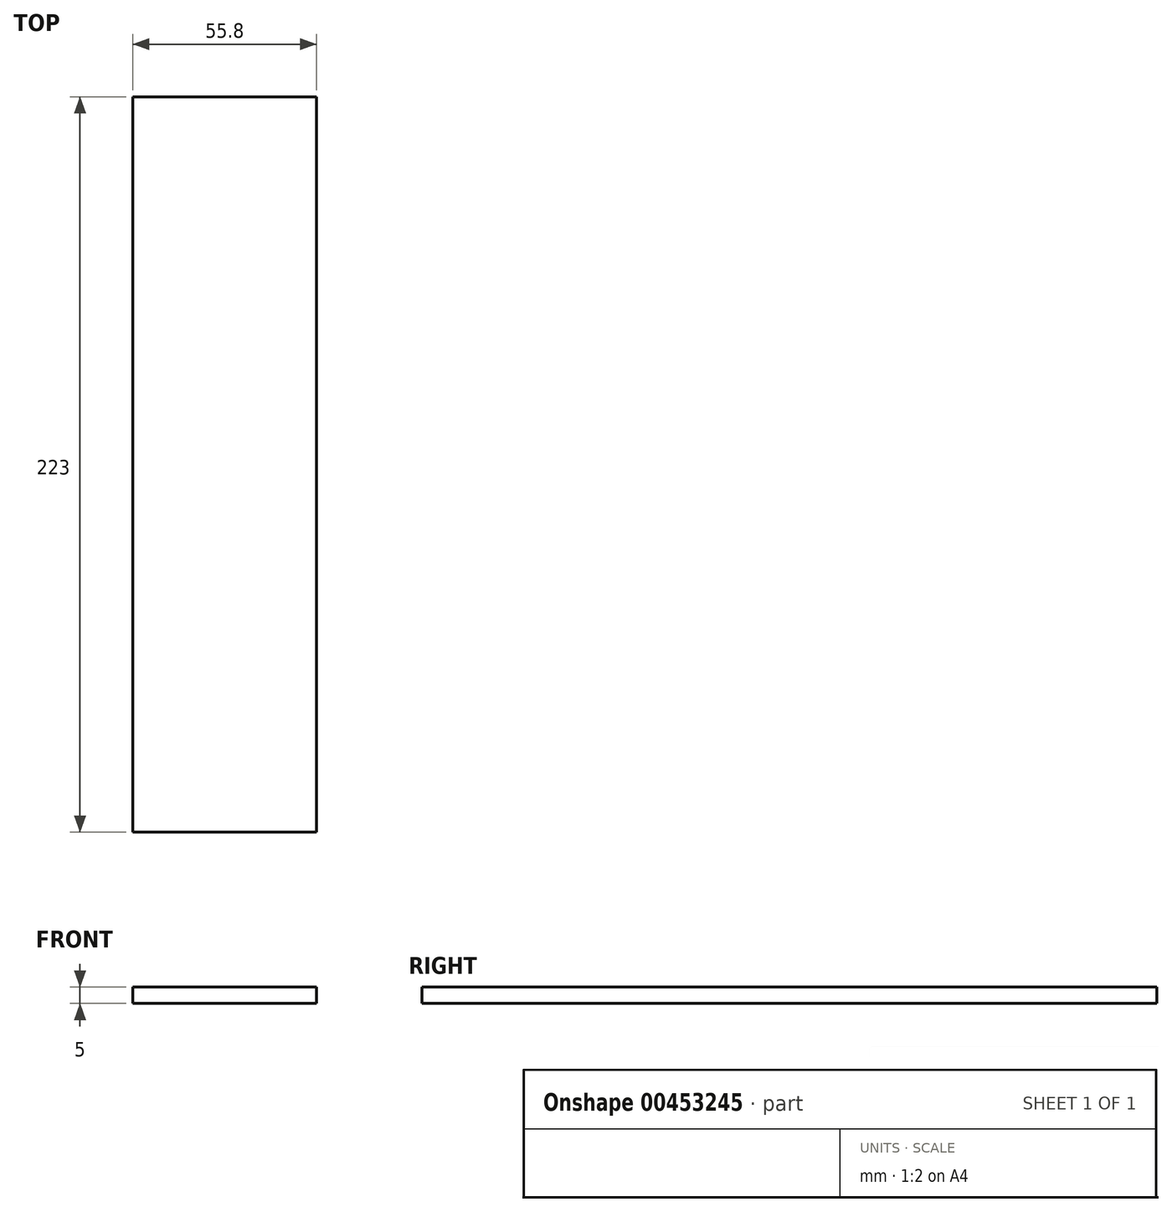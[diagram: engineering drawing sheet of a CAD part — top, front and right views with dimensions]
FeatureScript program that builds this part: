
annotation { "Feature Type Name" : "Feature", "Feature Type Description" : "" }
export const myFeature = defineFeature(function(context is Context, id is Id, definition is map)
    precondition{}
    {
        {
            var Q0;
            Q0=qCreatedBy(makeId("Top.planeOp"),FACE);
            var sketch = newSketch(context, id + "F0", { "sketchPlane" : qUnion([Q0])});
            skLineSegment(sketch, "E0.bottom", {"start": v(27.9, -111.5) * mm, "end": v(-27.9, -111.5) * mm});
            skLineSegment(sketch, "E0.top", {"start": v(27.9, 111.5) * mm, "end": v(-27.9, 111.5) * mm});
            skLineSegment(sketch, "E0.left", {"start": v(27.9, -111.5) * mm, "end": v(27.9, 111.5) * mm});
            skLineSegment(sketch, "E0.right", {"start": v(-27.9, -111.5) * mm, "end": v(-27.9, 111.5) * mm});
            skPoint(sketch, "E0.middle", {"position": v(0, 0) * mm});
            skLineSegment(sketch, "E1.bottom", {"start": v(-8.06, 111.5) * mm, "end": v(2.88, 111.5) * mm});
            skLineSegment(sketch, "E1.top", {"start": v(-8.06, 111.5) * mm, "end": v(2.88, 111.5) * mm});
            skLineSegment(sketch, "E1.left", {"start": v(-8.06, 111.5) * mm, "end": v(-8.06, 111.5) * mm});
            skLineSegment(sketch, "E1.right", {"start": v(2.88, 111.5) * mm, "end": v(2.88, 111.5) * mm});
            skPoint(sketch, "E1.middle", {"position": v(-2.6, 111.5) * mm});
            skSolve(sketch);
        }
        {
            var Q0;
            Q0=makeQuery(id+"F0.imprint","IMPRINT",FACE,{"disambiguationData":[TD([[makeQuery(id+"F0.imprint","IMPRINT",EDGE,{"derivedFrom":sQuery(id+"F0.wireOp",EDGE,"E0.bottom")}),-1.0]])]});
            var Q1;
            Q1=sQuery(id+"F0.wireOp",EDGE,"E0.top");
            var Q2;
            Q2=sQuery(id+"F0.wireOp",EDGE,"E0.right");
            var Q3;
            Q3=sQuery(id+"F0.wireOp",EDGE,"E0.bottom");
            var Q4;
            Q4=sQuery(id+"F0.wireOp",EDGE,"E0.left");
            extrude(context, id + "F1", {"entities" : qUnion([Q0]), "surfaceEntities" : qUnion([Q1, Q2, Q3, Q4]), "depth" : 5 * mm});
        }
    });
